# Revit family: Bicycle-Rack_Dero_UltraSpaceSaver-Floor
name_source: partatom
category: Generic Models
units: mm (PartAtom-declared; Revit-internal decimal feet)

## family parameters
Can host rebar = No
Classification Number = 23.40.10.11.11
Cut with Voids When Loaded = No
Host = Face
Maintain Annotation Orientation = No
Part Type = Normal
Room Calculation Point = No
Round Connector Dimension = Use Diameter
Shared = No

## types (6) — shared parameters
Assembly Code = E1090900
Available Options = Galvanized / Powder Coat  ;  Wheel Stop
CAD Details = https://www.arcat.com
Capacity = 1 Bike per Ear
Default Elevation = 0' - 0"
Keynote = 12 93 13
Manufacturer = Dero Bike Rack Co.
Product Page URL = https://www.arcat.com
Specification = https://www.arcat.com
URL = http://www.dero.com
Unit Height = 6' - 9"
zero-valued in all types: Cost

## per-type parameters (varying)
| type | Circle | Description | Double Sided | Foot Front Length | Foot Rear Length | Height to First Crossbeam | LowerMount | Model | Rack Type | Square |
| Double Sided Angled Space Saver Squared | No | Dero Floor Mounted Bike Rack - Ultra Space Saver Squared Angled as Specified | Yes | 2' - 3" | 2' - 3" | 3' - 10 29/32" | 2' - 9 13/32" | Ultra Space Saver Squared Angled DS | Ear : Angled Square Ear | Yes |
| Double Sided Space Saver Squared | No | Dero Floor Mounted Bike Rack - Ultra Space Saver Squared as Specified | Yes | 2' - 3" | 2' - 3" | 3' - 10 29/32" | 2' - 9 13/32" | Ultra Space Saver Squared DS | Ear : Square Ear | Yes |
| Double Sided Space Saver | Yes | Dero Floor Mounted Bike Rack - Ultra Space Saver as Specified | Yes | 2' - 3" | 2' - 3" | 3' - 11 3/16" | 2' - 9 11/16" | Ultra Space Saver DS | Ear : Circle Ear | No |
| Single Sided Angled Space Saver Squared | No | Dero Floor Mounted Bike Rack - Ultra Space Saver Squared Angled as Specified | No | 2' - 3 1/8" | 0' - 2 3/4" | 3' - 10 29/32" | 2' - 9 13/32" | Ultra Space Saver Squared Angled | Ear : Angled Square Ear | Yes |
| Single Sided Space Saver Squared | No | Dero Floor Mounted Bike Rack - Ultra Space Saver Squared as Specified | No | 2' - 3 1/8" | 0' - 2 3/4" | 3' - 10 29/32" | 2' - 9 13/32" | Ultra Space Saver Squared | Ear : Square Ear | Yes |
| Single Sided Space Saver | Yes | Dero Floor Mounted Bike Rack - Ultra Space Saver as Specified | No | 2' - 3 1/8" | 0' - 2 3/4" | 3' - 11 3/16" | 2' - 9 11/16" | Ultra Space Saver | Ear : Circle Ear | No |

## geometry (parser evidence)
native form markers: Sweep x11
no freeform markers — native parametric forms only
